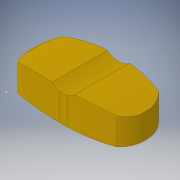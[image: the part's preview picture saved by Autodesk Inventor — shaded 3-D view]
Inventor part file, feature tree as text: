
AUTODESK INVENTOR PART (.ipt)
format: ipt  version: 2019 (Build 230136000, 136)  size: 214,528 bytes
history: native  units: in
note: dims shown in document units (in); Inventor stores cm internally (conversion verified against a paired STEP export)
features: sketch x8, extrude x7
ambient origin geometry x8: Origin, YZ Plane, XZ Plane, XY Plane, X Axis, Y Axis, Z Axis, Center Point
bodies: Solid1 (feature_tree)
feature tree (15):
  extrude  "Extrusion1"  Depth=1.9685in
  extrude  "Extrusion2"  Depth=0.9843in
  sketch  "Sketch3"  dims[d4=0.189in d5=2.984in]
  extrude  "Extrusion3"  Depth=2.984in
  extrude  "Extrusion4"  Depth=0.1181in
  extrude  "Extrusion5"  Depth=0.3937in
  extrude  "Extrusion6"  Depth=1.1063in TaperAngle=0.0deg
  extrude  "Extrusion7"  Depth=0.3937in
  sketch  "Sketch1"  dims[d0=3.937in d1=1.9685in]
  sketch  "Sketch2"  dims[d2=0.9843in d3=0.4764in]
  sketch  "Sketch4"  dims[d6=0.189in d7=0.1181in]
  sketch  "Sketch5"  dims[d8=0.3937in d9=0.0in d10=0.0787in]
  sketch  "Sketch6"  dims[d11=0.7205in d12=0.0in d13=1.1063in d14=0.0in]
  sketch  "Sketch7"  dims[d15=0.3937in d16=0.3937in]
  sketch  "Sketch8"  dims[d17=0.5906in d18=1.9685in d19=0.0in d20=1.9685in d21=0.0in d22=1.9685in d23=0.0in d24=1.9685in d25=0.0in]
